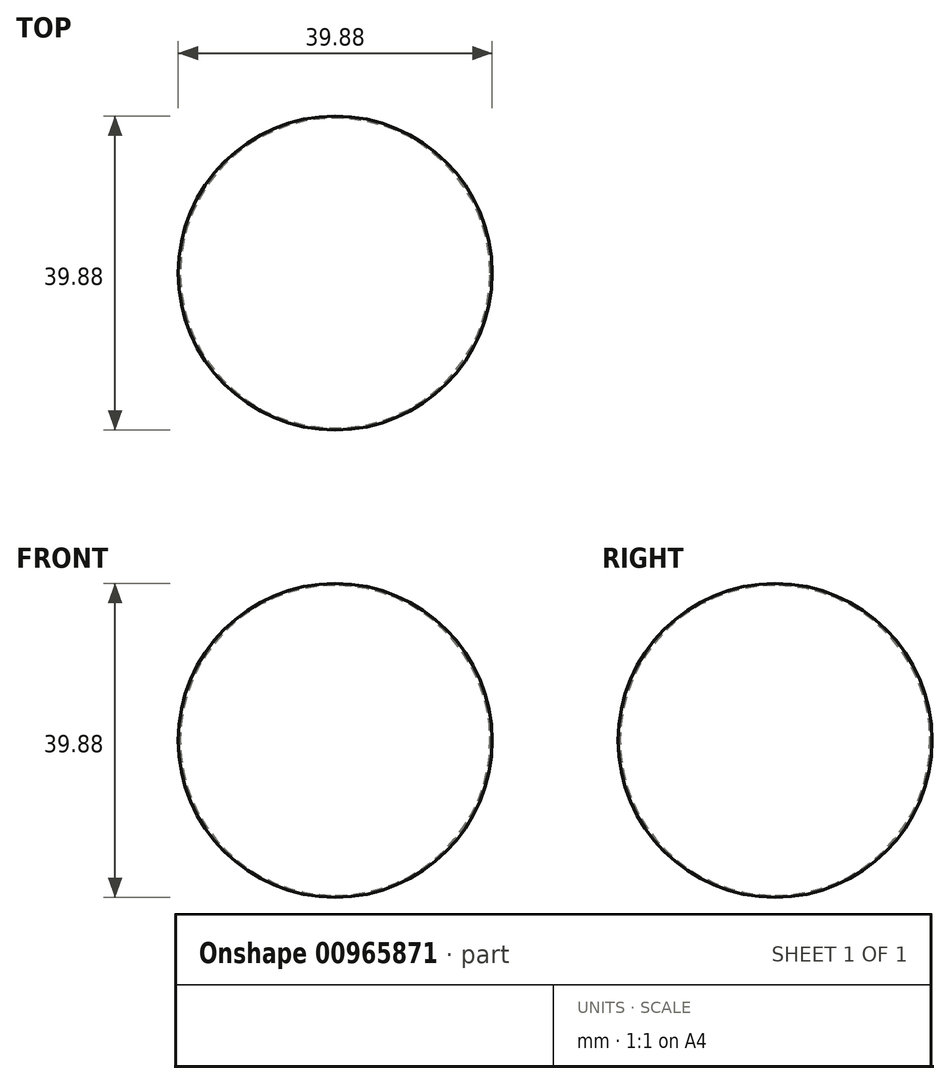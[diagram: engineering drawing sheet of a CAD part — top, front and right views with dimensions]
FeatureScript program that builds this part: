
annotation { "Feature Type Name" : "Feature", "Feature Type Description" : "" }
export const myFeature = defineFeature(function(context is Context, id is Id, definition is map)
    precondition{}
    {
        {
            var Q0;
            Q0=qCreatedBy(makeId("Front.planeOp"),FACE);
            var sketch = newSketch(context, id + "F0", { "sketchPlane" : qUnion([Q0])});
            skArc(sketch, "E0", {"start": v(0, -19.94) * mm, "mid": v(19.94, 0) * mm, "end": v(0, 19.94) * mm});
            skArc(sketch, "E1", {"start": v(0, -19.69) * mm, "mid": v(19.69, 0) * mm, "end": v(0, 19.69) * mm});
            skLineSegment(sketch, "E2", {"start": v(0, 19.94) * mm, "end": v(0, -19.94) * mm});
            skSolve(sketch);
        }
        {
            var Q0;
            {var subQ0=sQuery(id+"F0.wireOp",EDGE,"E0");Q0=makeQuery(id+"F0.imprint","IMPRINT",FACE,{"disambiguationData":[TD([[makeQuery(id+"F0.imprint","IMPRINT",EDGE,{"derivedFrom":subQ0}),1.0]])]});}
            var Q1;
            Q1=sQuery(id+"F0.wireOp",EDGE,"E2");
            revolve(context, id + "F1", {"surfaceOperationType" : NewSurfaceOperationType.NEW, "entities" : qUnion([Q0]), "axis" : qUnion([Q1]), "revolveType" : RevolveType.FULL});
        }
    });
